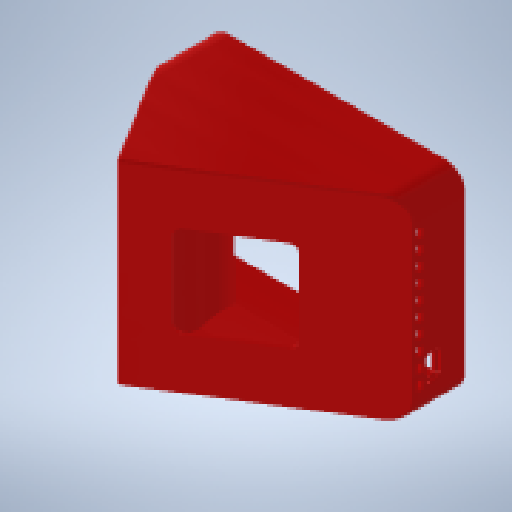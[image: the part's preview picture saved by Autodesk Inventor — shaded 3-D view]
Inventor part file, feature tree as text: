
AUTODESK INVENTOR PART (.ipt)
format: ipt  version: 2023.1 (Build 271208000, 208)  size: 1,425,408 bytes
history: native  units: mm
features: chamfer x23, extrude x19, delete_face x19, projected_geometry x19, sketch x18, reference x9, other x6, plane x2, direct_edit x1, fillet x1, move_body x1
ambient origin geometry x8: Origin, YZ Plane, XZ Plane, XY Plane, X Axis, Y Axis, Z Axis, Center Point
bodies: Volumenkörper1 (feature_tree)
feature tree (118):
  extrude  "Extrusion1"  Depth=0.1mm
  extrude  "Extrusion2"  Depth=0.1mm
  sketch  "Skizze3"  dims[d5=0.1mm d6=2.0mm d7=0.0mm]
  plane  "Arbeitsebene1"
  extrude  "Extrusion3"  Depth=2.0mm TaperAngle=0.0deg
  sketch  "Skizze4"  dims[d8=1.0mm d9=1.0mm]
  plane  "Arbeitsebene2"
  extrude  "Extrusion4"  Depth=1.0mm
  chamfer  "Fase1"  [1 undecoded]
  chamfer  "Fase2"  Distance=29.0mm
  chamfer  "Fase3"  Distance=8.0mm
  chamfer  "Fase4"  Distance=4.0mm Angle=45.0deg
  chamfer  "Fase5"  Distance=0.4mm Angle=45.0deg
  chamfer  "Fase6"  Distance=0.8mm Angle=45.0deg
  extrude  "Extrusion5"  Depth=10.0mm TaperAngle=45.0deg
  sketch  "Skizze7"  dims[d11=1.0mm d12=0.0mm d13=0.0mm]
  extrude  "Extrusion6"  Depth=10.0mm TaperAngle=45.0deg
  extrude  "Extrusion7"  Depth=10.0mm TaperAngle=45.0deg
  extrude  "Extrusion8"  Depth=10.0mm TaperAngle=0.0deg
  extrude  "Extrusion9"  Depth=10.0mm
  chamfer  "Fase8"  Distance=1.6mm
  extrude  "Extrusion10"  Depth=10.0mm
  delete_face  "Fläche löschen1"
  extrude  "Extrusion11"  Depth=10.0mm
  delete_face  "Fläche löschen2"
  delete_face  "Fläche löschen3"
  delete_face  "Fläche löschen4"
  delete_face  "Fläche löschen5"
  extrude  "Extrusion12"  Depth=10.0mm
  chamfer  "Fase9"  Distance=1.2mm
  chamfer  "Fase10"  Distance=10.12291mm
  chamfer  "Fase11"  Distance=1.0mm
  chamfer  "Fase12"  [1 undecoded]
  chamfer  "Fase13"  Distance=20.5mm
  extrude  "Extrusion13"  Depth=10.0mm
  extrude  "Extrusion14"  TaperAngle=0.0deg  [1 undecoded]
  chamfer  "Fase14"  Distance=3.9mm
  delete_face  "Fläche löschen6"
  chamfer  "Fase15"  Distance=9.6mm
  chamfer  "Fase16"  Distance=1.3mm
  direct_edit  "Direktbearbeitung1"
  extrude  "Extrusion15"  Depth=10.0mm
  extrude  "Extrusion16"  Depth=10.0mm
  extrude  "Extrusion17"  Depth=10.0mm TaperAngle=0.0deg
  chamfer  "Fase17"  Distance=0.6mm Angle=45.0deg
  extrude  "Extrusion18"  Depth=10.0mm
  delete_face  "Fläche löschen7"
  fillet  "Rundung1"  Radius=1.6mm
  delete_face  "Fläche löschen8"
  delete_face  "Fläche löschen9"
  extrude  "Extrusion19"  Depth=10.0mm
  delete_face  "Fläche löschen10"
  delete_face  "Fläche löschen11"
  delete_face  "Fläche löschen12"
  chamfer  "Fase18"  Distance=1.6mm
  delete_face  "Fläche löschen13"
  delete_face  "Fläche löschen14"
  delete_face  "Fläche löschen15"
  chamfer  "Fase19"  Distance=0.4mm
  chamfer  "Fase20"  Distance=10.0mm
  chamfer  "Fase21"  Distance=30.0mm
  delete_face  "Fläche löschen16"
  delete_face  "Fläche löschen17"
  delete_face  "Fläche löschen18"
  chamfer  "Fase22"  Distance=10.0mm
  chamfer  "Fase23"  Distance=2.0mm Angle=45.0deg
  chamfer  "Fase24"  Distance=0.8mm Angle=45.0deg
  delete_face  "Fläche löschen19"
  sketch  "Skizze1"  dims[d0=0.1mm d1=0.1mm]
  reference  "Referenz1"
  sketch  "Skizze2"  dims[d2=0.1mm d3=0.1mm]
  reference  "Referenz2"
  projected_geometry  "Projizierte Kontur1"
  reference  "Referenz3"
  reference  "Referenz4"
  reference  "Referenz5"
  reference  "Referenz6"
  reference  "Referenz7"
  reference  "Referenz8"
  sketch  "Skizze6"  dims[d10=1.0mm]
  projected_geometry  "Projizierte Kontur2"
  sketch  "Skizze9"  dims[d14=2.0mm]
  sketch  "Skizze10"  dims[d15=2.0mm]
  projected_geometry  "Projizierte Kontur6"
  sketch  "Skizze11"  dims[d16=2.0mm]
  projected_geometry  "Projizierte Kontur7"
  sketch  "Skizze12"  dims[d17=2.0mm]
  sketch  "Skizze13"  dims[d19=2.0mm d20=29.0mm d21=0.0mm]
  projected_geometry  "Projizierte Kontur8"
  projected_geometry  "Projizierte Kontur9"
  projected_geometry  "Projizierte Kontur10"
  projected_geometry  "Projizierte Kontur11"
  projected_geometry  "Projizierte Kontur12"
  projected_geometry  "Projizierte Kontur13"
  projected_geometry  "Projizierte Kontur14"
  projected_geometry  "Projizierte Kontur15"
  projected_geometry  "Projizierte Kontur16"
  sketch  "Skizze14"  dims[d22=1.21mm]
  sketch  "Skizze15"  dims[d23=4.42mm]
  projected_geometry  "Projizierte Kontur17"
  projected_geometry  "Projizierte Kontur18"
  sketch  "Skizze16"  dims[d24=4.42mm]
  projected_geometry  "Projizierte Kontur19"
  sketch  "Skizze17"  dims[d25=4.42mm]
  reference  "Referenz10"
  sketch  "Skizze18"  dims[d26=4.42mm]
  sketch  "Skizze19"  dims[d27=4.42mm]
  projected_geometry  "Projizierte Kontur20"
  projected_geometry  "Projizierte Kontur21"
  sketch  "Skizze20"  dims[d28=4.42mm d29=8.0mm d30=0.0mm d31=4.0mm d32=2.0mm d33=45.0deg d34=0.4mm d35=2.0mm d36=45.0deg d37=0.8mm d38=2.0mm d39=45.0deg d40=0.8mm d41=2.0mm d42=45.0deg d43=0.8mm d44=2.0mm d45=45.0deg d46=0.4mm d47=2.0mm d48=45.0deg d55=3.0mm d56=0.0mm d57=1.6mm d58=1.6mm d59=1.6mm d60=1.6mm d62=1.6mm d63=1.2mm d64=0.0mm d67=10.12291mm d68=1.0mm d69=0.0mm d70=0.0mm d71=20.5mm d72=23.0mm d73=0.0mm d74=0.0mm d75=3.9mm d76=9.6mm d77=1.3mm d78=14.4mm d79=15.2mm d83=0.4mm d84=0.0mm d85=0.6mm d86=2.0mm d87=45.0deg d88=1.6mm d89=1.6mm d90=6.0mm d92=1.6mm d93=0.4mm d94=0.0mm d95=10.0mm d96=0.0mm d97=30.0mm d98=10.0mm d99=0.0mm d100=2.0mm d101=2.0mm d102=45.0deg d103=0.8mm d104=2.0mm d105=45.0deg d106=1.2mm d107=2.0mm d108=45.0deg d109=0.4mm d110=2.0mm d111=45.0deg d112=1.0mm d113=2.0mm d114=45.0deg d115=30.0mm d116=0.0mm d117=13.4mm d118=10.0mm d119=0.0mm d120=1.2mm d121=0.0mm d122=0.4mm d123=2.0mm d124=45.0deg d125=2.0mm d126=2.0mm d127=45.0deg d128=0.8mm d129=2.0mm d130=45.0deg d131=0.0mm d132=0.0mm d133=0.8mm d134=4.6mm d135=8.6mm d136=4.6mm d137=8.6mm d138=4.6mm d139=8.6mm d140=4.6mm d141=8.6mm d142=0.0mm d143=65.799279mm d144=40.0mm d145=16.899639mm d146=80.0mm d147=0.8mm d148=0.0mm d149=0.0mm d150=0.0mm d151=10.0mm d152=0.0mm d153=0.4mm d154=2.0mm d155=45.0deg d156=1.4mm d157=2.2mm d158=4.0mm d159=2.881818mm d160=2.881818mm d161=4.0mm d162=2.881818mm d163=4.0mm d164=2.881818mm d165=4.0mm d166=2.881818mm d167=2.881818mm d168=2.881818mm d169=4.0mm d170=4.0mm d171=4.0mm d172=2.881818mm d173=2.881818mm d174=4.0mm d175=4.0mm d176=2.881818mm d177=4.0mm d178=2.881818mm d179=4.0mm d180=0.0mm d181=8.0mm d182=4.0mm d183=0.0mm d184=2.0mm d185=2.0mm d186=45.0deg d187=2.0mm d188=2.0mm d189=45.0deg d190=2.0mm d191=2.0mm d192=45.0deg d193=2.0mm d194=2.0mm d195=45.0deg d196=0.399mm d197=2.0mm d198=45.0deg d199=1.0mm d200=2.0mm d201=45.0deg d202=2.0mm d203=2.0mm d204=45.0deg]
  projected_geometry  "Projizierte Kontur22"
  other  "<userpath>\Desktop\GitHub\Voron-2-Mods\Misc\ISDT C4 EVO\CAD\Isdt.iam"
  other  "Isdt.iam"
  other  "Isdt_Dummy:1"
  move_body  "Verschieben1"
  other  "<userpath>\Desktop\CAD\ISDT C4Evo\V2.iam"
  other  "V2.iam"
  other  "FanCover - Kopie:1"
note: 3 required parameter values undecoded (feature->parameter linkage not recoverable at this tier; creation-order binding heuristic only, values carry confidence <= 0.55)
